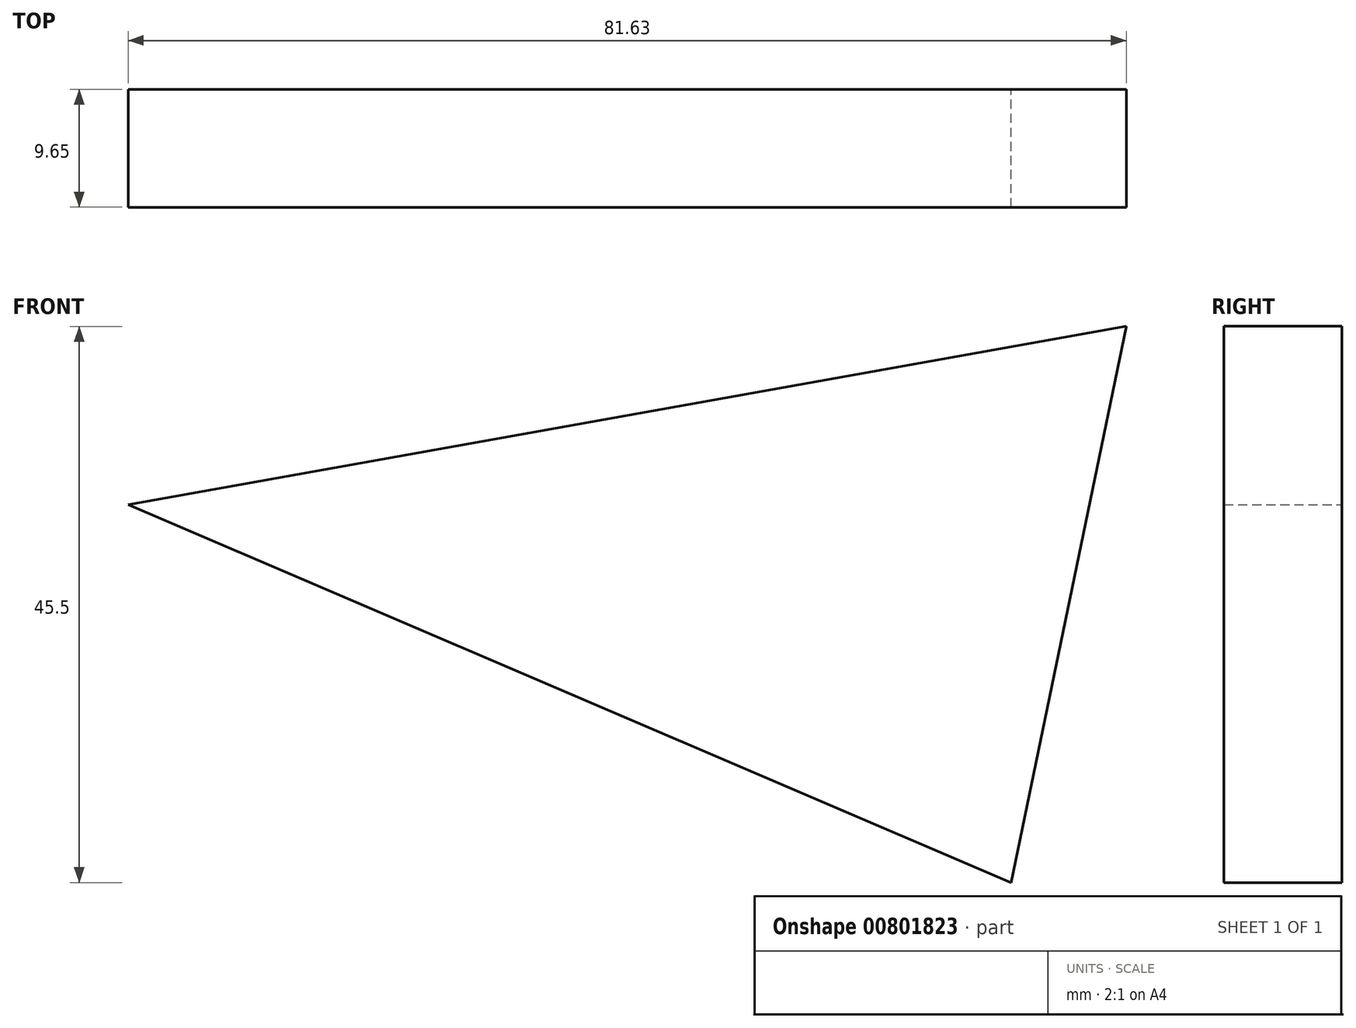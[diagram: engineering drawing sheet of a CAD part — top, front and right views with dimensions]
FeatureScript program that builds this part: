
annotation { "Feature Type Name" : "Feature", "Feature Type Description" : "" }
export const myFeature = defineFeature(function(context is Context, id is Id, definition is map)
    precondition{}
    {
        {
            var Q0;
            Q0=qCreatedBy(makeId("Front.planeOp"),FACE);
            var sketch = newSketch(context, id + "F0", { "sketchPlane" : qUnion([Q0])});
            skLineSegment(sketch, "E0", {"start": v(55.19, 57.15) * mm, "end": v(-26.44, 42.55) * mm});
            skLineSegment(sketch, "E1", {"start": v(-26.44, 42.55) * mm, "end": v(45.76, 11.65) * mm});
            skLineSegment(sketch, "E2", {"start": v(45.76, 11.65) * mm, "end": v(55.19, 57.15) * mm});
            skSolve(sketch);
        }
        {
            var Q0;
            Q0=makeQuery(id+"F0.imprint","IMPRINT",FACE,{"disambiguationData":[TD([[makeQuery(id+"F0.imprint","IMPRINT",EDGE,{"derivedFrom":sQuery(id+"F0.wireOp",EDGE,"E0")}),1.0]])]});
            extrude(context, id + "F1", {"entities" : qUnion([Q0]), "depth" : 9.65 * mm, "offsetDistance" : 25.4 * mm});
        }
    });
